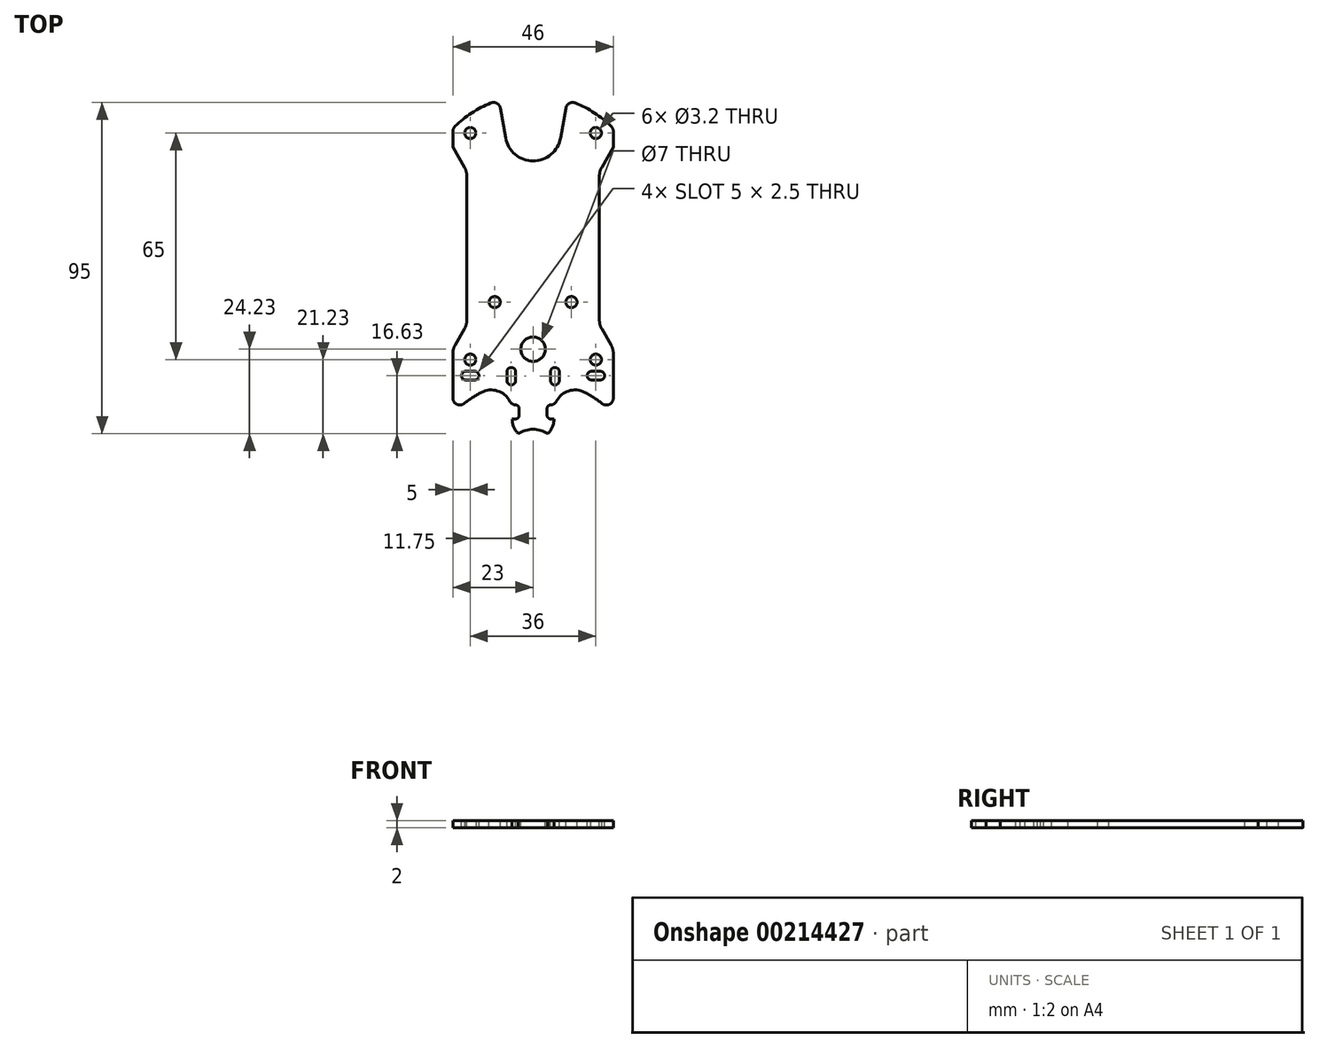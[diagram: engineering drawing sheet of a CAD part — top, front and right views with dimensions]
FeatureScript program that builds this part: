
annotation { "Feature Type Name" : "Feature", "Feature Type Description" : "" }
export const myFeature = defineFeature(function(context is Context, id is Id, definition is map)
    precondition{}
    {
        {
            var Q0;
            Q0=qCreatedBy(makeId("Top.planeOp"),FACE);
            var sketch = newSketch(context, id + "F0", { "sketchPlane" : qUnion([Q0])});
            skLineSegment(sketch, "E0.left", {"start": v(-23, 37.42) * mm, "end": v(-23, -39.03) * mm});
            skLineSegment(sketch, "E0.right", {"start": v(23, 37.42) * mm, "end": v(23, -39.03) * mm});
            skArc(sketch, "E1", {"start": v(22.4, 38.85) * mm, "mid": v(17.58, 42.74) * mm, "end": v(12.1, 45.62) * mm});
            skArc(sketch, "E2", {"start": v(19.76, -40.6) * mm, "mid": v(17.34, -38.87) * mm, "end": v(14.77, -37.38) * mm});
            skPoint(sketch, "E3.visualSharp", {"position": v(-23, 38.25) * mm});
            skArc(sketch, "E3.filletArc", {"start": v(-22.4, 38.85) * mm, "mid": v(-22.84, 38.2) * mm, "end": v(-23, 37.42) * mm});
            skPoint(sketch, "E4.visualSharp", {"position": v(23, 38.25) * mm});
            skArc(sketch, "E4.filletArc", {"start": v(23, 37.42) * mm, "mid": v(22.84, 38.2) * mm, "end": v(22.4, 38.85) * mm});
            skPoint(sketch, "E5.visualSharp", {"position": v(-23, -43.52) * mm});
            skArc(sketch, "E5.filletArc", {"start": v(-23, -39.03) * mm, "mid": v(-21.87, -40.82) * mm, "end": v(-19.76, -40.6) * mm});
            skPoint(sketch, "E6.visualSharp", {"position": v(23, -43.52) * mm});
            skArc(sketch, "E6.filletArc", {"start": v(19.76, -40.6) * mm, "mid": v(21.87, -40.82) * mm, "end": v(23, -39.03) * mm});
            skCircle(sketch, "E7", {"center": v(-18, 37) * mm, "radius": 1.6 * mm});
            skCircle(sketch, "E8", {"center": v(-18, -28) * mm, "radius": 1.6 * mm});
            skCircle(sketch, "E9.MirrorC", {"center": v(18, 37) * mm, "radius": 1.6 * mm});
            skCircle(sketch, "E10.MirrorC", {"center": v(18, -28) * mm, "radius": 1.6 * mm});
            skArc(sketch, "E11", {"start": v(-7.88, 35.61) * mm, "mid": v(0, 29) * mm, "end": v(7.88, 35.61) * mm});
            skLineSegment(sketch, "E12", {"start": v(-7.88, 35.61) * mm, "end": v(-9.38, 44.12) * mm});
            skLineSegment(sketch, "E13", {"start": v(7.88, 35.61) * mm, "end": v(9.38, 44.12) * mm});
            skArc(sketch, "E14.trimOffspring", {"start": v(-12.1, 45.62) * mm, "mid": v(-17.58, 42.74) * mm, "end": v(-22.4, 38.85) * mm});
            skPoint(sketch, "E15.visualSharp", {"position": v(-9.8, 46.46) * mm});
            skArc(sketch, "E15.filletArc", {"start": v(-9.38, 44.12) * mm, "mid": v(-10.38, 45.52) * mm, "end": v(-12.1, 45.62) * mm});
            skPoint(sketch, "E16.visualSharp", {"position": v(9.8, 46.46) * mm});
            skArc(sketch, "E16.filletArc", {"start": v(12.1, 45.62) * mm, "mid": v(10.38, 45.52) * mm, "end": v(9.38, 44.12) * mm});
            skLineSegment(sketch, "E17.left", {"start": v(-6, -42.7) * mm, "end": v(-6, -45) * mm});
            skLineSegment(sketch, "E17.right", {"start": v(6, -42.7) * mm, "end": v(6, -45) * mm});
            skArc(sketch, "E18", {"start": v(-6, -45) * mm, "mid": v(0, -51) * mm, "end": v(6, -45) * mm});
            skArc(sketch, "E19.trimOffspring", {"start": v(-14.77, -37.38) * mm, "mid": v(-17.34, -38.87) * mm, "end": v(-19.76, -40.6) * mm});
            skPoint(sketch, "E20.visualSharp", {"position": v(-6, -34.33) * mm});
            skArc(sketch, "E20.filletArc", {"start": v(-6, -42.7) * mm, "mid": v(-8.89, -37.57) * mm, "end": v(-14.77, -37.38) * mm});
            skPoint(sketch, "E21.visualSharp", {"position": v(6, -34.33) * mm});
            skArc(sketch, "E21.filletArc", {"start": v(14.77, -37.38) * mm, "mid": v(8.89, -37.57) * mm, "end": v(6, -42.7) * mm});
            skSolve(sketch);
        }
        {
            var Q0;
            Q0 = qSketchRegion(id + "F0", true);
            extrude(context, id + "F1", {"entities" : qUnion([Q0]), "depth" : 2 * mm});
        }
        {
            var Q0;
            Q0=makeQuery(id+"F1.opExtrude","CAP_FACE",FACE,{"disambiguationData":[OSD([sQuery(id+"F0.wireOp",EDGE,"E0.left"),sQuery(id+"F0.wireOp",EDGE,"E0.right"),sQuery(id+"F0.wireOp",EDGE,"E1"),sQuery(id+"F0.wireOp",EDGE,"E2"),sQuery(id+"F0.wireOp",EDGE,"E3.filletArc"),sQuery(id+"F0.wireOp",EDGE,"E4.filletArc"),sQuery(id+"F0.wireOp",EDGE,"E5.filletArc"),sQuery(id+"F0.wireOp",EDGE,"E6.filletArc"),sQuery(id+"F0.wireOp",EDGE,"E7"),sQuery(id+"F0.wireOp",EDGE,"E8"),sQuery(id+"F0.wireOp",EDGE,"E9.MirrorC"),sQuery(id+"F0.wireOp",EDGE,"E10.MirrorC"),sQuery(id+"F0.wireOp",EDGE,"E11"),sQuery(id+"F0.wireOp",EDGE,"E12"),sQuery(id+"F0.wireOp",EDGE,"E13"),sQuery(id+"F0.wireOp",EDGE,"E14.trimOffspring"),sQuery(id+"F0.wireOp",EDGE,"E15.filletArc"),sQuery(id+"F0.wireOp",EDGE,"E16.filletArc"),sQuery(id+"F0.wireOp",EDGE,"E17.left"),sQuery(id+"F0.wireOp",EDGE,"E17.right"),sQuery(id+"F0.wireOp",EDGE,"E18"),sQuery(id+"F0.wireOp",EDGE,"E19.trimOffspring"),sQuery(id+"F0.wireOp",EDGE,"E20.filletArc"),sQuery(id+"F0.wireOp",EDGE,"E21.filletArc")])],"isStart":false});
            var sketch = newSketch(context, id + "F2", { "sketchPlane" : qUnion([Q0])});
            skLineSegment(sketch, "E22.bottom", {"start": v(-10, -41) * mm, "end": v(-4, -41) * mm});
            skLineSegment(sketch, "E22.top", {"start": v(-10, -45) * mm, "end": v(-4, -45) * mm});
            skLineSegment(sketch, "E22.left", {"start": v(-10, -41) * mm, "end": v(-10, -45) * mm});
            skLineSegment(sketch, "E22.right", {"start": v(-4, -41) * mm, "end": v(-4, -45) * mm});
            skLineSegment(sketch, "E23.bottom", {"start": v(10, -45) * mm, "end": v(4, -45) * mm});
            skLineSegment(sketch, "E23.top", {"start": v(10, -41) * mm, "end": v(4, -41) * mm});
            skLineSegment(sketch, "E23.left", {"start": v(10, -45) * mm, "end": v(10, -41) * mm});
            skLineSegment(sketch, "E23.right", {"start": v(4, -45) * mm, "end": v(4, -41) * mm});
            skLineSegment(sketch, "E24.bottom", {"start": v(-5, -31.5) * mm, "end": v(-7.5, -31.5) * mm, "construction": true});
            skLineSegment(sketch, "E24.top", {"start": v(-5, -34) * mm, "end": v(-7.5, -34) * mm, "construction": true});
            skLineSegment(sketch, "E24.left", {"start": v(-5, -31.5) * mm, "end": v(-5, -34) * mm});
            skLineSegment(sketch, "E24.right", {"start": v(-7.5, -31.5) * mm, "end": v(-7.5, -34) * mm});
            skLineSegment(sketch, "E25.bottom", {"start": v(5, -31.5) * mm, "end": v(7.5, -31.5) * mm, "construction": true});
            skLineSegment(sketch, "E25.top", {"start": v(5, -34) * mm, "end": v(7.5, -34) * mm, "construction": true});
            skLineSegment(sketch, "E25.left", {"start": v(5, -31.5) * mm, "end": v(5, -34) * mm});
            skLineSegment(sketch, "E25.right", {"start": v(7.5, -31.5) * mm, "end": v(7.5, -34) * mm});
            skArc(sketch, "E26", {"start": v(-7.5, -34) * mm, "mid": v(-6.25, -35.25) * mm, "end": v(-5, -34) * mm});
            skArc(sketch, "E27", {"start": v(-5, -31.5) * mm, "mid": v(-6.25, -30.25) * mm, "end": v(-7.5, -31.5) * mm});
            skPoint(sketch, "E28.midSnap0", {"position": v(6.25, -31.5) * mm});
            skPoint(sketch, "E28.midSnap1", {"position": v(-6.25, -30.25) * mm});
            skArc(sketch, "E29", {"start": v(5, -34) * mm, "mid": v(6.25, -35.25) * mm, "end": v(7.5, -34) * mm});
            skArc(sketch, "E30", {"start": v(7.5, -31.5) * mm, "mid": v(6.25, -30.25) * mm, "end": v(5, -31.5) * mm});
            skCircle(sketch, "E31", {"center": v(-11, -11.5) * mm, "radius": 1.6 * mm});
            skCircle(sketch, "E32", {"center": v(11, -11.5) * mm, "radius": 1.6 * mm});
            skCircle(sketch, "E33", {"center": v(0, -25) * mm, "radius": 3.5 * mm});
            skCircle(sketch, "E34", {"center": v(0, -56) * mm, "radius": 8 * mm});
            skSolve(sketch);
        }
        {
            var Q0;
            Q0 = qSketchRegion(id + "F2", true);
            extrude(context, id + "F3", {"entities" : qUnion([Q0]), "operationType" : NewBodyOperationType.REMOVE, "endBound" : BoundingType.THROUGH_ALL, "oppositeDirection" : true, "depth" : 25 * mm});
        }
        {
            var Q0;
            Q0=makeQuery(id+"F1.opExtrude","CAP_FACE",FACE,{"disambiguationData":[OSD([sQuery(id+"F0.wireOp",EDGE,"E0.left"),sQuery(id+"F0.wireOp",EDGE,"E0.right"),sQuery(id+"F0.wireOp",EDGE,"E1"),sQuery(id+"F0.wireOp",EDGE,"E2"),sQuery(id+"F0.wireOp",EDGE,"E3.filletArc"),sQuery(id+"F0.wireOp",EDGE,"E4.filletArc"),sQuery(id+"F0.wireOp",EDGE,"E5.filletArc"),sQuery(id+"F0.wireOp",EDGE,"E6.filletArc"),sQuery(id+"F0.wireOp",EDGE,"E7"),sQuery(id+"F0.wireOp",EDGE,"E8"),sQuery(id+"F0.wireOp",EDGE,"E9.MirrorC"),sQuery(id+"F0.wireOp",EDGE,"E10.MirrorC"),sQuery(id+"F0.wireOp",EDGE,"E11"),sQuery(id+"F0.wireOp",EDGE,"E12"),sQuery(id+"F0.wireOp",EDGE,"E13"),sQuery(id+"F0.wireOp",EDGE,"E14.trimOffspring"),sQuery(id+"F0.wireOp",EDGE,"E15.filletArc"),sQuery(id+"F0.wireOp",EDGE,"E16.filletArc"),sQuery(id+"F0.wireOp",EDGE,"E17.left"),sQuery(id+"F0.wireOp",EDGE,"E17.right"),sQuery(id+"F0.wireOp",EDGE,"E18"),sQuery(id+"F0.wireOp",EDGE,"E19.trimOffspring"),sQuery(id+"F0.wireOp",EDGE,"E20.filletArc"),sQuery(id+"F0.wireOp",EDGE,"E21.filletArc")])],"isStart":false});
            var sketch = newSketch(context, id + "F4", { "sketchPlane" : qUnion([Q0])});
            skLineSegment(sketch, "E35.right", {"start": v(-19, 24.66) * mm, "end": v(-19, -16.66) * mm});
            skLineSegment(sketch, "E36.right", {"start": v(19, 24.66) * mm, "end": v(19, -16.66) * mm});
            skLineSegment(sketch, "E37", {"start": v(-23, 32.93) * mm, "end": v(-19.67, 27.16) * mm});
            skLineSegment(sketch, "E38", {"start": v(23, 32.93) * mm, "end": v(19.67, 27.16) * mm});
            skLineSegment(sketch, "E39", {"start": v(-19.67, -19.16) * mm, "end": v(-23, -24.93) * mm});
            skLineSegment(sketch, "E40", {"start": v(19.67, -19.16) * mm, "end": v(23, -24.93) * mm});
            skPoint(sketch, "E41.visualSharp", {"position": v(-19, 26) * mm});
            skArc(sketch, "E41.filletArc", {"start": v(-19, 24.66) * mm, "mid": v(-19.17, 25.95) * mm, "end": v(-19.67, 27.16) * mm});
            skPoint(sketch, "E42.visualSharp", {"position": v(-19, -18) * mm});
            skArc(sketch, "E42.filletArc", {"start": v(-19.67, -19.16) * mm, "mid": v(-19.17, -17.95) * mm, "end": v(-19, -16.66) * mm});
            skPoint(sketch, "E43.visualSharp", {"position": v(19, -18) * mm});
            skArc(sketch, "E43.filletArc", {"start": v(19, -16.66) * mm, "mid": v(19.17, -17.95) * mm, "end": v(19.67, -19.16) * mm});
            skPoint(sketch, "E44.visualSharp", {"position": v(19, 26) * mm});
            skArc(sketch, "E44.filletArc", {"start": v(19.67, 27.16) * mm, "mid": v(19.17, 25.95) * mm, "end": v(19, 24.66) * mm});
            skLineSegment(sketch, "E45", {"start": v(-23, 32.93) * mm, "end": v(-23, -24.93) * mm});
            skLineSegment(sketch, "E46", {"start": v(23, 32.93) * mm, "end": v(23, -24.93) * mm});
            skSolve(sketch);
        }
        {
            var Q0;
            Q0 = qSketchRegion(id + "F4", true);
            extrude(context, id + "F5", {"entities" : qUnion([Q0]), "operationType" : NewBodyOperationType.REMOVE, "endBound" : BoundingType.THROUGH_ALL, "oppositeDirection" : true, "depth" : 25 * mm});
        }
        {
            var Q0;
            Q0=makeQuery(id+"F5.boolean.opBoolean","COPY",EDGE,{"derivedFrom":makeQuery(id+"F5.opExtrude","SWEPT_EDGE",EDGE,{"disambiguationData":[OSD([sQuery(id+"F0.wireOp",EDGE,"E0.left"),sQuery(id+"F4.wireOp",EDGE,"E37"),sQuery(id+"F4.wireOp",EDGE,"E45")])]})});
            var Q1;
            Q1=makeQuery(id+"F5.boolean.opBoolean","COPY",EDGE,{"derivedFrom":makeQuery(id+"F5.opExtrude","SWEPT_EDGE",EDGE,{"disambiguationData":[OSD([sQuery(id+"F0.wireOp",EDGE,"E0.right"),sQuery(id+"F4.wireOp",EDGE,"E38"),sQuery(id+"F4.wireOp",EDGE,"E46")])]})});
            var Q2;
            Q2=makeQuery(id+"F5.boolean.opBoolean","COPY",EDGE,{"derivedFrom":makeQuery(id+"F5.opExtrude","SWEPT_EDGE",EDGE,{"disambiguationData":[OSD([sQuery(id+"F0.wireOp",EDGE,"E0.right"),sQuery(id+"F4.wireOp",EDGE,"E40"),sQuery(id+"F4.wireOp",EDGE,"E46")])]})});
            var Q3;
            Q3=makeQuery(id+"F5.boolean.opBoolean","COPY",EDGE,{"derivedFrom":makeQuery(id+"F5.opExtrude","SWEPT_EDGE",EDGE,{"disambiguationData":[OSD([sQuery(id+"F0.wireOp",EDGE,"E0.left"),sQuery(id+"F4.wireOp",EDGE,"E39"),sQuery(id+"F4.wireOp",EDGE,"E45")])]})});
            fillet(context, id + "F6", {"entities" : qUnion([Q0, Q1, Q2, Q3]), "radius" : 5 * mm, "tangentPropagation" : true, "allowEdgeOverflow" : false});
        }
        {
            var Q0;
            Q0=makeQuery(id+"F3.boolean.opBoolean","COPY",EDGE,{"derivedFrom":makeQuery(id+"F3.opExtrude","SWEPT_EDGE",EDGE,{"disambiguationData":[OSD([sQuery(id+"F2.wireOp",EDGE,"E22.bottom"),sQuery(id+"F2.wireOp",EDGE,"E22.right")])]})});
            var Q1;
            Q1=makeQuery(id+"F3.boolean.opBoolean","COPY",EDGE,{"derivedFrom":makeQuery(id+"F3.opExtrude","SWEPT_EDGE",EDGE,{"disambiguationData":[OSD([sQuery(id+"F2.wireOp",EDGE,"E22.top"),sQuery(id+"F2.wireOp",EDGE,"E22.right")])]})});
            var Q2;
            Q2=makeQuery(id+"F3.boolean.opBoolean","COPY",EDGE,{"derivedFrom":makeQuery(id+"F3.opExtrude","SWEPT_EDGE",EDGE,{"disambiguationData":[OSD([sQuery(id+"F2.wireOp",EDGE,"E23.top"),sQuery(id+"F2.wireOp",EDGE,"E23.right")])]})});
            var Q3;
            Q3=makeQuery(id+"F3.boolean.opBoolean","COPY",EDGE,{"derivedFrom":makeQuery(id+"F3.opExtrude","SWEPT_EDGE",EDGE,{"disambiguationData":[OSD([sQuery(id+"F2.wireOp",EDGE,"E23.bottom"),sQuery(id+"F2.wireOp",EDGE,"E23.right")])]})});
            fillet(context, id + "F7", {"entities" : qUnion([Q0, Q1, Q2, Q3]), "radius" : 1 * mm, "tangentPropagation" : true, "allowEdgeOverflow" : false});
        }
        {
            var Q0;
            Q0=makeQuery(id+"F3.boolean.opBoolean","INTERSECT",EDGE,{"derivedFrom":[makeQuery(id+"F1.opExtrude","SWEPT_FACE",FACE,{"disambiguationData":[OSD([sQuery(id+"F0.wireOp",EDGE,"E20.filletArc")])]}),makeQuery(id+"F3.opExtrude","SWEPT_FACE",FACE,{"disambiguationData":[OSD([sQuery(id+"F2.wireOp",EDGE,"E22.bottom")])]})]});
            var Q1;
            Q1=makeQuery(id+"F3.boolean.opBoolean","INTERSECT",EDGE,{"derivedFrom":[makeQuery(id+"F1.opExtrude","SWEPT_FACE",FACE,{"disambiguationData":[OSD([sQuery(id+"F0.wireOp",EDGE,"E21.filletArc")])]}),makeQuery(id+"F3.opExtrude","SWEPT_FACE",FACE,{"disambiguationData":[OSD([sQuery(id+"F2.wireOp",EDGE,"E23.top")])]})]});
            var Q2;
            Q2=makeQuery(id+"F1.opExtrude","SWEPT_EDGE",EDGE,{"disambiguationData":[OSD([sQuery(id+"F0.wireOp",EDGE,"E17.left"),sQuery(id+"F0.wireOp",EDGE,"E18")])]});
            var Q3;
            Q3=makeQuery(id+"F1.opExtrude","SWEPT_EDGE",EDGE,{"disambiguationData":[OSD([sQuery(id+"F0.wireOp",EDGE,"E17.right"),sQuery(id+"F0.wireOp",EDGE,"E18")])]});
            fillet(context, id + "F8", {"entities" : qUnion([Q0, Q1, Q2, Q3]), "radius" : 2 * mm, "tangentPropagation" : true, "allowEdgeOverflow" : false});
        }
        {
            var Q0;
            Q0=makeQuery(id+"F1.opExtrude","CAP_FACE",FACE,{"disambiguationData":[OSD([sQuery(id+"F0.wireOp",EDGE,"E0.left"),sQuery(id+"F0.wireOp",EDGE,"E0.right"),sQuery(id+"F0.wireOp",EDGE,"E1"),sQuery(id+"F0.wireOp",EDGE,"E2"),sQuery(id+"F0.wireOp",EDGE,"E3.filletArc"),sQuery(id+"F0.wireOp",EDGE,"E4.filletArc"),sQuery(id+"F0.wireOp",EDGE,"E5.filletArc"),sQuery(id+"F0.wireOp",EDGE,"E6.filletArc"),sQuery(id+"F0.wireOp",EDGE,"E7"),sQuery(id+"F0.wireOp",EDGE,"E8"),sQuery(id+"F0.wireOp",EDGE,"E9.MirrorC"),sQuery(id+"F0.wireOp",EDGE,"E10.MirrorC"),sQuery(id+"F0.wireOp",EDGE,"E11"),sQuery(id+"F0.wireOp",EDGE,"E12"),sQuery(id+"F0.wireOp",EDGE,"E13"),sQuery(id+"F0.wireOp",EDGE,"E14.trimOffspring"),sQuery(id+"F0.wireOp",EDGE,"E15.filletArc"),sQuery(id+"F0.wireOp",EDGE,"E16.filletArc"),sQuery(id+"F0.wireOp",EDGE,"E17.left"),sQuery(id+"F0.wireOp",EDGE,"E17.right"),sQuery(id+"F0.wireOp",EDGE,"E18"),sQuery(id+"F0.wireOp",EDGE,"E19.trimOffspring"),sQuery(id+"F0.wireOp",EDGE,"E20.filletArc"),sQuery(id+"F0.wireOp",EDGE,"E21.filletArc")])],"isStart":false});
            var sketch = newSketch(context, id + "F9", { "sketchPlane" : qUnion([Q0])});
            skLineSegment(sketch, "E47.bottom", {"start": v(-16.75, -31.35) * mm, "end": v(-19.25, -31.35) * mm});
            skLineSegment(sketch, "E47.top", {"start": v(-16.75, -33.85) * mm, "end": v(-19.25, -33.85) * mm});
            skLineSegment(sketch, "E47.left", {"start": v(-16.75, -31.35) * mm, "end": v(-16.75, -33.85) * mm, "construction": true});
            skLineSegment(sketch, "E47.right", {"start": v(-19.25, -31.35) * mm, "end": v(-19.25, -33.85) * mm, "construction": true});
            skArc(sketch, "E48", {"start": v(-19.25, -31.35) * mm, "mid": v(-20.5, -32.6) * mm, "end": v(-19.25, -33.85) * mm});
            skArc(sketch, "E49", {"start": v(-16.75, -33.85) * mm, "mid": v(-15.5, -32.6) * mm, "end": v(-16.75, -31.35) * mm});
            skLineSegment(sketch, "E50.MirrorCS", {"start": v(16.75, -31.35) * mm, "end": v(19.25, -31.35) * mm});
            skLineSegment(sketch, "E51.MirrorCS", {"start": v(16.75, -33.85) * mm, "end": v(19.25, -33.85) * mm});
            skLineSegment(sketch, "E52.MirrorCS", {"start": v(19.25, -31.35) * mm, "end": v(19.25, -33.85) * mm, "construction": true});
            skLineSegment(sketch, "E53.MirrorCS", {"start": v(16.75, -31.35) * mm, "end": v(16.75, -33.85) * mm, "construction": true});
            skArc(sketch, "E54.MirrorCS", {"start": v(19.25, -31.35) * mm, "mid": v(20.5, -32.6) * mm, "end": v(19.25, -33.85) * mm});
            skArc(sketch, "E55.MirrorCS", {"start": v(16.75, -33.85) * mm, "mid": v(15.5, -32.6) * mm, "end": v(16.75, -31.35) * mm});
            skSolve(sketch);
        }
        {
            var Q0;
            Q0 = qSketchRegion(id + "F9", true);
            extrude(context, id + "F10", {"entities" : qUnion([Q0]), "operationType" : NewBodyOperationType.REMOVE, "endBound" : BoundingType.THROUGH_ALL, "oppositeDirection" : true, "depth" : 25 * mm});
        }
    });
